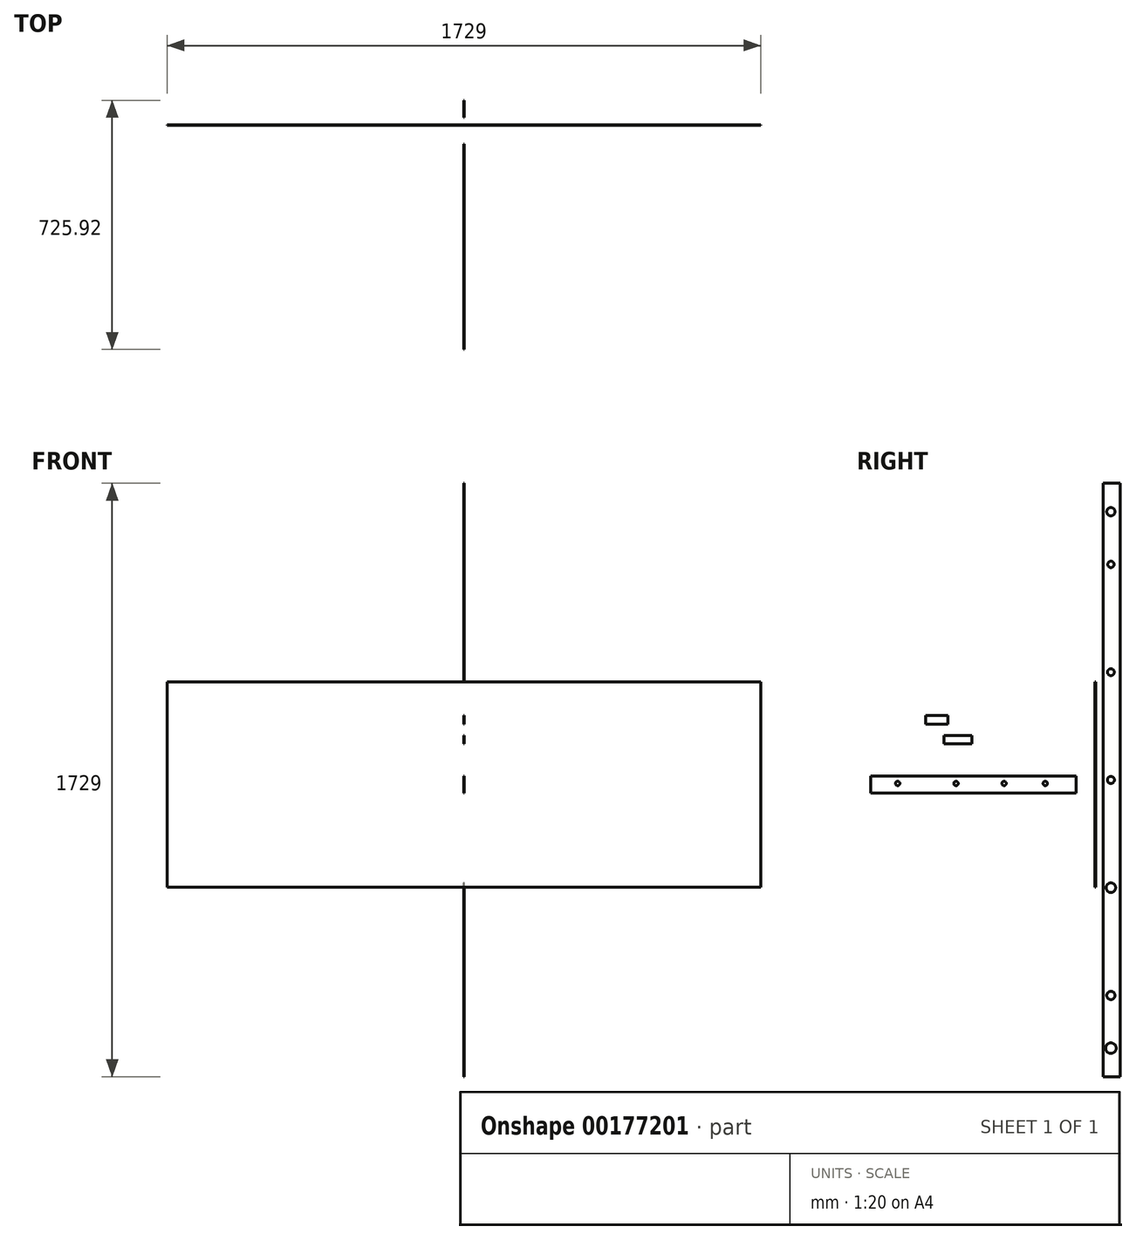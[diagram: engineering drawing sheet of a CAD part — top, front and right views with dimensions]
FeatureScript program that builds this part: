
annotation { "Feature Type Name" : "Feature", "Feature Type Description" : "" }
export const myFeature = defineFeature(function(context is Context, id is Id, definition is map)
    precondition{}
    {
        {
            var Q0;
            Q0=qCreatedBy(makeId("Front.planeOp"),FACE);
            var sketch = newSketch(context, id + "F0", { "sketchPlane" : qUnion([Q0])});
            skLineSegment(sketch, "E0.bottom", {"start": v(864.5, 299) * mm, "end": v(-864.5, 299) * mm});
            skLineSegment(sketch, "E0.top", {"start": v(864.5, -299) * mm, "end": v(-864.5, -299) * mm});
            skLineSegment(sketch, "E0.left", {"start": v(864.5, 299) * mm, "end": v(864.5, -299) * mm});
            skLineSegment(sketch, "E0.right", {"start": v(-864.5, 299) * mm, "end": v(-864.5, -299) * mm});
            skPoint(sketch, "E0.middle", {"position": v(0, 0) * mm});
            skSolve(sketch);
        }
        {
            var Q0;
            Q0=makeQuery(id+"F0.imprint","IMPRINT",FACE,{"disambiguationData":[TD([[makeQuery(id+"F0.imprint","IMPRINT",EDGE,{"derivedFrom":sQuery(id+"F0.wireOp",EDGE,"E0.bottom")}),1.0]])]});
            extrude(context, id + "F1", {"entities" : qUnion([Q0]), "oppositeDirection" : true, "depth" : 2 * mm});
        }
        {
            var Q0;
            Q0=qCreatedBy(makeId("Right.planeOp"),FACE);
            var sketch = newSketch(context, id + "F2", { "sketchPlane" : qUnion([Q0])});
            skLineSegment(sketch, "E1.bottom", {"start": v(-54.64, 25) * mm, "end": v(-652.64, 25) * mm});
            skLineSegment(sketch, "E1.top", {"start": v(-54.64, -25) * mm, "end": v(-652.64, -25) * mm});
            skLineSegment(sketch, "E1.left", {"start": v(-54.64, 25) * mm, "end": v(-54.64, -25) * mm});
            skLineSegment(sketch, "E1.right", {"start": v(-652.64, 25) * mm, "end": v(-652.64, -25) * mm});
            skPoint(sketch, "E1.middle", {"position": v(-353.64, 0) * mm});
            skCircle(sketch, "E2", {"center": v(-574.64, 3) * mm, "radius": 6.35 * mm});
            skCircle(sketch, "E3", {"center": v(-404.64, 3) * mm, "radius": 6.35 * mm});
            skCircle(sketch, "E4", {"center": v(-264.64, 3) * mm, "radius": 6.35 * mm});
            skCircle(sketch, "E5", {"center": v(-144.64, 3) * mm, "radius": 6.35 * mm});
            skSolve(sketch);
        }
        {
            var Q0;
            Q0=makeQuery(id+"F2.imprint","IMPRINT",FACE,{"disambiguationData":[TD([[makeQuery(id+"F2.imprint","IMPRINT",EDGE,{"derivedFrom":sQuery(id+"F2.wireOp",EDGE,"E1.bottom")}),1.0]])]});
            extrude(context, id + "F3", {"entities" : qUnion([Q0]), "endBound" : BoundingType.SYMMETRIC, "depth" : 2 * mm});
        }
        {
            var Q0;
            Q0=qCreatedBy(makeId("Right.planeOp"),FACE);
            var sketch = newSketch(context, id + "F4", { "sketchPlane" : qUnion([Q0])});
            skLineSegment(sketch, "E6.bottom", {"start": v(23.28, -851.26) * mm, "end": v(73.28, -851.26) * mm});
            skLineSegment(sketch, "E6.top", {"start": v(23.28, 877.74) * mm, "end": v(73.28, 877.74) * mm});
            skLineSegment(sketch, "E6.left", {"start": v(23.28, -851.26) * mm, "end": v(23.28, 877.74) * mm});
            skLineSegment(sketch, "E6.right", {"start": v(73.28, -851.26) * mm, "end": v(73.28, 877.74) * mm});
            skPoint(sketch, "E6.middle", {"position": v(48.28, 13.24) * mm});
            skCircle(sketch, "E7", {"center": v(46.28, 794.74) * mm, "radius": 12.04 * mm});
            skCircle(sketch, "E8", {"center": v(46.28, 641.24) * mm, "radius": 9.25 * mm});
            skCircle(sketch, "E9", {"center": v(46.28, 327.24) * mm, "radius": 10.06 * mm});
            skCircle(sketch, "E10", {"center": v(46.28, 13.24) * mm, "radius": 10.29 * mm});
            skCircle(sketch, "E11", {"center": v(46.28, -300.76) * mm, "radius": 14 * mm});
            skCircle(sketch, "E12", {"center": v(46.28, -614.76) * mm, "radius": 12.1 * mm});
            skCircle(sketch, "E13", {"center": v(46.28, -768.26) * mm, "radius": 15.43 * mm});
            skSolve(sketch);
        }
        {
            var Q0;
            Q0=makeQuery(id+"F4.imprint","IMPRINT",FACE,{"disambiguationData":[TD([[makeQuery(id+"F4.imprint","IMPRINT",EDGE,{"derivedFrom":sQuery(id+"F4.wireOp",EDGE,"E6.bottom")}),1.0]])]});
            extrude(context, id + "F5", {"entities" : qUnion([Q0]), "endBound" : BoundingType.SYMMETRIC, "depth" : 2 * mm});
        }
        {
            var Q0;
            Q0=qCreatedBy(makeId("Right.planeOp"),FACE);
            var sketch = newSketch(context, id + "F6", { "sketchPlane" : qUnion([Q0])});
            skLineSegment(sketch, "E14.bottom", {"start": v(-427.83, 175.84) * mm, "end": v(-492.83, 175.84) * mm});
            skLineSegment(sketch, "E14.top", {"start": v(-427.83, 200.84) * mm, "end": v(-492.83, 200.84) * mm});
            skLineSegment(sketch, "E14.left", {"start": v(-427.83, 175.84) * mm, "end": v(-427.83, 200.84) * mm});
            skLineSegment(sketch, "E14.right", {"start": v(-492.83, 175.84) * mm, "end": v(-492.83, 200.84) * mm});
            skPoint(sketch, "E14.middle", {"position": v(-460.33, 188.34) * mm});
            skSolve(sketch);
        }
        {
            var Q0;
            Q0=makeQuery(id+"F6.imprint","IMPRINT",FACE,{"disambiguationData":[TD([[makeQuery(id+"F6.imprint","IMPRINT",EDGE,{"derivedFrom":sQuery(id+"F6.wireOp",EDGE,"E14.bottom")}),-1.0]])]});
            extrude(context, id + "F7", {"entities" : qUnion([Q0]), "endBound" : BoundingType.SYMMETRIC, "depth" : 2 * mm});
        }
        {
            var Q0;
            Q0=qCreatedBy(makeId("Right.planeOp"),FACE);
            var sketch = newSketch(context, id + "F8", { "sketchPlane" : qUnion([Q0])});
            skLineSegment(sketch, "E15.bottom", {"start": v(-358.35, 118.28) * mm, "end": v(-439.35, 118.28) * mm});
            skLineSegment(sketch, "E15.top", {"start": v(-358.35, 143.28) * mm, "end": v(-439.35, 143.28) * mm});
            skLineSegment(sketch, "E15.left", {"start": v(-358.35, 118.28) * mm, "end": v(-358.35, 143.28) * mm});
            skLineSegment(sketch, "E15.right", {"start": v(-439.35, 118.28) * mm, "end": v(-439.35, 143.28) * mm});
            skPoint(sketch, "E15.middle", {"position": v(-398.85, 130.78) * mm});
            skSolve(sketch);
        }
        {
            var Q0;
            Q0=makeQuery(id+"F8.imprint","IMPRINT",FACE,{"disambiguationData":[TD([[makeQuery(id+"F8.imprint","IMPRINT",EDGE,{"derivedFrom":sQuery(id+"F8.wireOp",EDGE,"E15.bottom")}),-1.0]])]});
            extrude(context, id + "F9", {"entities" : qUnion([Q0]), "endBound" : BoundingType.SYMMETRIC, "depth" : 2 * mm});
        }
    });
